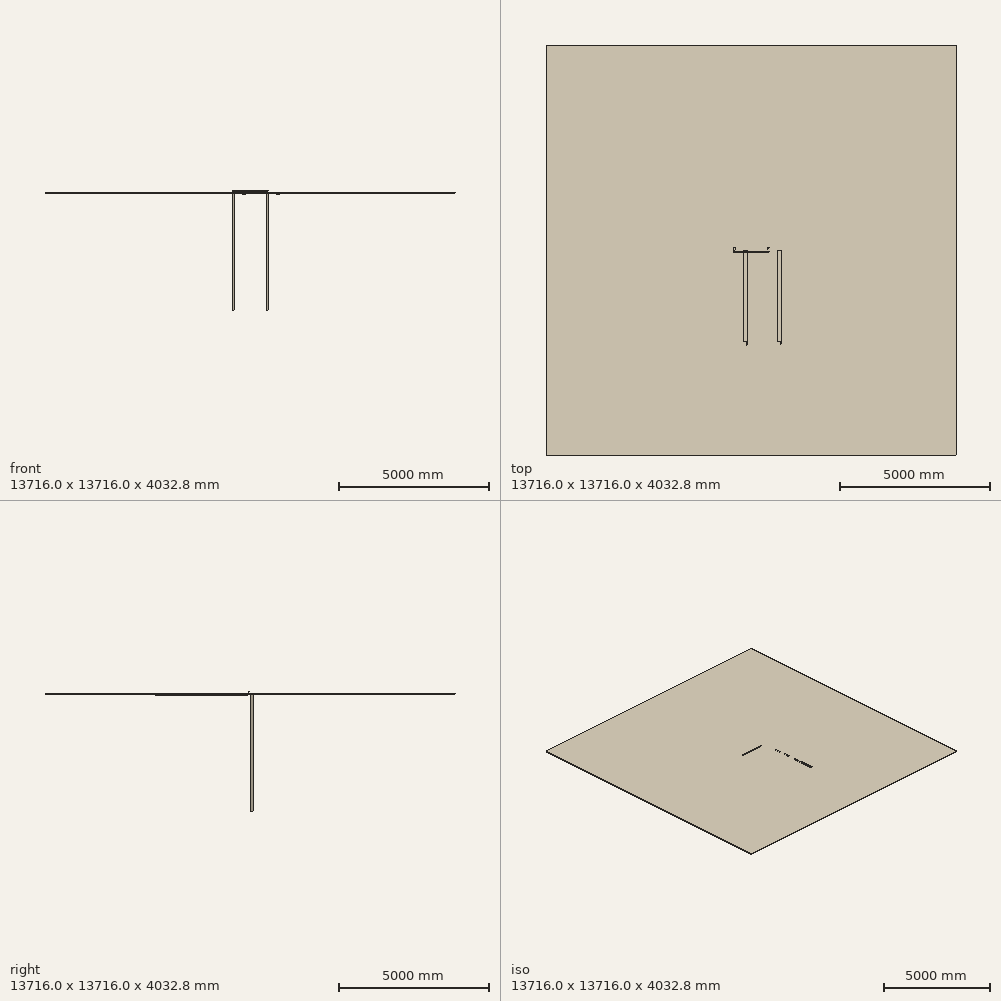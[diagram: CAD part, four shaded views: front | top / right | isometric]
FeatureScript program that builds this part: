
annotation { "Feature Type Name" : "Feature", "Feature Type Description" : "" }
export const myFeature = defineFeature(function(context is Context, id is Id, definition is map)
    precondition{}
    {
        {
            var Q0;
            Q0=qCreatedBy(makeId("Top.planeOp"),FACE);
            var sketch = newSketch(context, id + "F0", { "sketchPlane" : qUnion([Q0])});
            skLineSegment(sketch, "E0.bottom", {"start": v(520.7, 0) * mm, "end": v(609.6, 0) * mm});
            skLineSegment(sketch, "E0.top", {"start": v(520.7, 88.9) * mm, "end": v(609.6, 88.9) * mm});
            skLineSegment(sketch, "E0.left", {"start": v(520.7, 0) * mm, "end": v(520.7, 88.9) * mm});
            skLineSegment(sketch, "E0.right", {"start": v(609.6, 0) * mm, "end": v(609.6, 88.9) * mm});
            skLineSegment(sketch, "E1.bottom", {"start": v(-520.7, 0) * mm, "end": v(-609.6, 0) * mm});
            skLineSegment(sketch, "E1.top", {"start": v(-520.7, 88.9) * mm, "end": v(-609.6, 88.9) * mm});
            skLineSegment(sketch, "E1.left", {"start": v(-520.7, 0) * mm, "end": v(-520.7, 88.9) * mm});
            skLineSegment(sketch, "E1.right", {"start": v(-609.6, 0) * mm, "end": v(-609.6, 88.9) * mm});
            skSolve(sketch);
        }
        {
            var Q0;
            Q0 = qSketchRegion(id + "F0", true);
            extrude(context, id + "F1", {"entities" : qUnion([Q0]), "oppositeDirection" : true, "depth" : 3962.4 * mm});
        }
        {
            var Q0;
            Q0=qCreatedBy(makeId("Right.planeOp"),FACE);
            var sketch = newSketch(context, id + "F2", { "sketchPlane" : qUnion([Q0])});
            skCircle(sketch, "E2", {"center": v(-44.21, 44.96) * mm, "radius": 25.4 * mm});
            skSolve(sketch);
        }
        {
            var Q0;
            Q0=makeQuery(id+"F2.imprint","IMPRINT",FACE,{"disambiguationData":[TD([[makeQuery(id+"F2.imprint","IMPRINT",EDGE,{"derivedFrom":sQuery(id+"F2.wireOp",EDGE,"E2")}),1.0]])]});
            extrude(context, id + "F3", {"entities" : qUnion([Q0]), "endBound" : BoundingType.SYMMETRIC, "depth" : 1219.2 * mm});
        }
        {
            var Q0;
            Q0=qCreatedBy(makeId("Front.planeOp"),FACE);
            var sketch = newSketch(context, id + "F4", { "sketchPlane" : qUnion([Q0])});
            skLineSegment(sketch, "E3.bottom", {"start": v(871.84, 0) * mm, "end": v(960.74, 0) * mm});
            skLineSegment(sketch, "E3.top", {"start": v(871.84, -88.9) * mm, "end": v(960.74, -88.9) * mm});
            skLineSegment(sketch, "E3.left", {"start": v(871.84, 0) * mm, "end": v(871.84, -88.9) * mm});
            skLineSegment(sketch, "E3.right", {"start": v(960.74, 0) * mm, "end": v(960.74, -88.9) * mm});
            skLineSegment(sketch, "E4.bottom", {"start": v(-169.56, 0) * mm, "end": v(-258.46, 0) * mm});
            skLineSegment(sketch, "E4.top", {"start": v(-169.56, -88.9) * mm, "end": v(-258.46, -88.9) * mm});
            skLineSegment(sketch, "E4.left", {"start": v(-169.56, 0) * mm, "end": v(-169.56, -88.9) * mm});
            skLineSegment(sketch, "E4.right", {"start": v(-258.46, 0) * mm, "end": v(-258.46, -88.9) * mm});
            skSolve(sketch);
        }
        {
            var Q0;
            Q0=makeQuery(id+"F4.imprint","IMPRINT",FACE,{"disambiguationData":[TD([[makeQuery(id+"F4.imprint","IMPRINT",EDGE,{"derivedFrom":sQuery(id+"F4.wireOp",EDGE,"E4.bottom")}),1.0]])]});
            var Q1;
            Q1=makeQuery(id+"F4.imprint","IMPRINT",FACE,{"disambiguationData":[TD([[makeQuery(id+"F4.imprint","IMPRINT",EDGE,{"derivedFrom":sQuery(id+"F4.wireOp",EDGE,"E3.bottom")}),-1.0]])]});
            extrude(context, id + "F5", {"entities" : qUnion([Q0, Q1]), "depth" : 3048 * mm});
        }
        {
            var Q0;
            Q0=makeQuery(id+"F5.opExtrude","SWEPT_FACE",FACE,{"disambiguationData":[OSD([sQuery(id+"F4.wireOp",EDGE,"E3.right")])]});
            var sketch = newSketch(context, id + "F6", { "sketchPlane" : qUnion([Q0])});
            skLineSegment(sketch, "E5", {"start": v(0, 0) * mm, "end": v(-88.9, -88.9) * mm});
            skLineSegment(sketch, "E6", {"start": v(-88.9, -88.9) * mm, "end": v(0, -88.9) * mm});
            skLineSegment(sketch, "E7", {"start": v(0, -88.9) * mm, "end": v(0, 0) * mm});
            skSolve(sketch);
        }
        {
            var Q0;
            Q0 = qSketchRegion(id + "F6", true);
            extrude(context, id + "F7", {"entities" : qUnion([Q0]), "operationType" : NewBodyOperationType.REMOVE, "oppositeDirection" : true, "depth" : 1524 * mm});
        }
        {
            var Q0;
            Q0=makeQuery(id+"F5.opExtrude","SWEPT_FACE",FACE,{"disambiguationData":[OSD([sQuery(id+"F4.wireOp",EDGE,"E3.right")])]});
            extrude(context, id + "F8", {"entities" : qUnion([Q0]), "depth" : 38.1 * mm});
        }
        {
            var Q0;
            Q0=makeQuery(id+"F5.opExtrude","SWEPT_FACE",FACE,{"disambiguationData":[OSD([sQuery(id+"F4.wireOp",EDGE,"E4.left")])]});
            extrude(context, id + "F9", {"entities" : qUnion([Q0]), "depth" : 38.1 * mm});
        }
        {
            var Q0;
            Q0=makeQuery(id+"F8.opExtrude","SWEPT_FACE",FACE,{"disambiguationData":[OSD([sQuery(id+"F4.wireOp",EDGE,"E3.right")])]});
            extrude(context, id + "F10", {"entities" : qUnion([Q0]), "operationType" : NewBodyOperationType.ADD, "depth" : 143.68 * mm});
        }
        {
            var Q0;
            Q0=makeQuery(id+"F9.opExtrude","SWEPT_FACE",FACE,{"disambiguationData":[OSD([sQuery(id+"F4.wireOp",EDGE,"E4.left")])]});
            extrude(context, id + "F11", {"entities" : qUnion([Q0]), "operationType" : NewBodyOperationType.ADD, "depth" : 143.68 * mm});
        }
        {
            var Q0;
            Q0=qCreatedBy(makeId("Top.planeOp"),FACE);
            var sketch = newSketch(context, id + "F12", { "sketchPlane" : qUnion([Q0])});
            skLineSegment(sketch, "E8.rect.bottom", {"start": v(6858, -6858) * mm, "end": v(-6858, -6858) * mm});
            skLineSegment(sketch, "E8.rect.top", {"start": v(6858, 6858) * mm, "end": v(-6858, 6858) * mm});
            skLineSegment(sketch, "E8.rect.left", {"start": v(6858, -6858) * mm, "end": v(6858, 6858) * mm});
            skLineSegment(sketch, "E8.rect.right", {"start": v(-6858, -6858) * mm, "end": v(-6858, 6858) * mm});
            skPoint(sketch, "E8.rect.middle", {"position": v(0, 0) * mm});
            skSolve(sketch);
        }
        {
            var Q0;
            Q0 = qSketchRegion(id + "F12", true);
            extrude(context, id + "F13", {"entities" : qUnion([Q0]), "oppositeDirection" : true, "depth" : 25.4 * mm});
        }
    });
